# Revit family: Knight XL KBX0400-1000
name_source: partatom
category: Mechanical Equipment
revit_build: Autodesk Revit 2017 (Build: 20190507_1515(x64)
units: mm (PartAtom-declared; Revit-internal decimal feet)

## family parameters
Always vertical = Yes
Cut with Voids When Loaded = No
OmniClass Number = 23.65.35.11.17
OmniClass Title = Thermodynamic Water Heaters
Part Type = Normal
Room Calculation Point = No
Round Connector Dimension = Use Radius
Shared = No
Work Plane-Based = No

## types (5) — shared parameters
Back Clearance Depth = 24"
Clearance Display = Yes
Condensate Drain Radius = 3/8"
Description = Knight XL Commercial Boiler
FUEL TYPE = NATURAL GAS
Front Clearance Depth = 24"
Fuel Type = Natural or LP
Left Clearance Depth = 0"
Manufacturer = Lochinvar
Right Clearance Depth = 0"
SES BIM Studio # = 20 0649 02
Top Clearance Depth = 24"
URL = https://www.lochinvar.com
Voltage/Control = 24
Voltage/Heater = 120V
WEIGHT = TBD

## per-type parameters (varying)
| type | AIR INLET SIZE | Air Inlet Radius | C_DEPTH | D_Unit Depth plus Water Outlet Length | E_Gas Conn Offset from Bottom | FLA | FLOW RATE (GPM) | FRICTION LOSS (FT HD) | F_Gas Conn Offset From Right | Flue Radius | GALLON CAPACITY | GAS CONN SIZE | Gas Conn Radius | INPUT RATE (BTUH) | MCA | VENT SIZE | WATER CONN SIZE | Water Conn Radius |
| KBX0400N | 4" | 2" | 33 1/2" | 42 1/2" | 29 3/4" | 3.0 | 38 | 10 | 20 1/4" | 2" | 4.4 | 1" | 1/2" | 399,000 | 3.8 | 4" | 2" | 1" |
| KBX0500N | 4" | 2" | 33 1/2" | 42 1/2" | 29 3/4" | 3.1 | 48 | 14 | 20 1/4" | 2" | 4.9 | 1" | 1/2" | 500,000 | 3.9 | 4" | 2" | 1" |
| KBX0650N | 4" | 2" | 42 1/2" | 53" | 30 1/2" | 3.3 | 62 | 16 | 15 1/4" | 2" | 6.2 | 1 1/4" | 5/8" | 650,000 | 4.1 | 4" | 2" | 1" |
| KBX0800N | 4" | 2" | 42 1/2" | 53" | 30 1/2" | 4.3 | 76 | 17 | 15 1/4" | 3" | 7.3 | 1 1/4" | 5/8" | 800,000 | 5.4 | 6" | 2" | 1" |
| KBX1000N | 6" | 3" | 50" | 62" | 30 1/2" | 6.6 | 96 | 18 | 15 3/4" | 3" | 8.8 | 1 1/4" | 5/8" | 999,000 | 8.3 | 6" | 2 1/2" | 1 1/4" |

note: column(s) folded — value = type name in every type: MODEL NO., Model

## geometry (parser evidence)
native form markers: Sweep x2
no freeform markers — native parametric forms only
